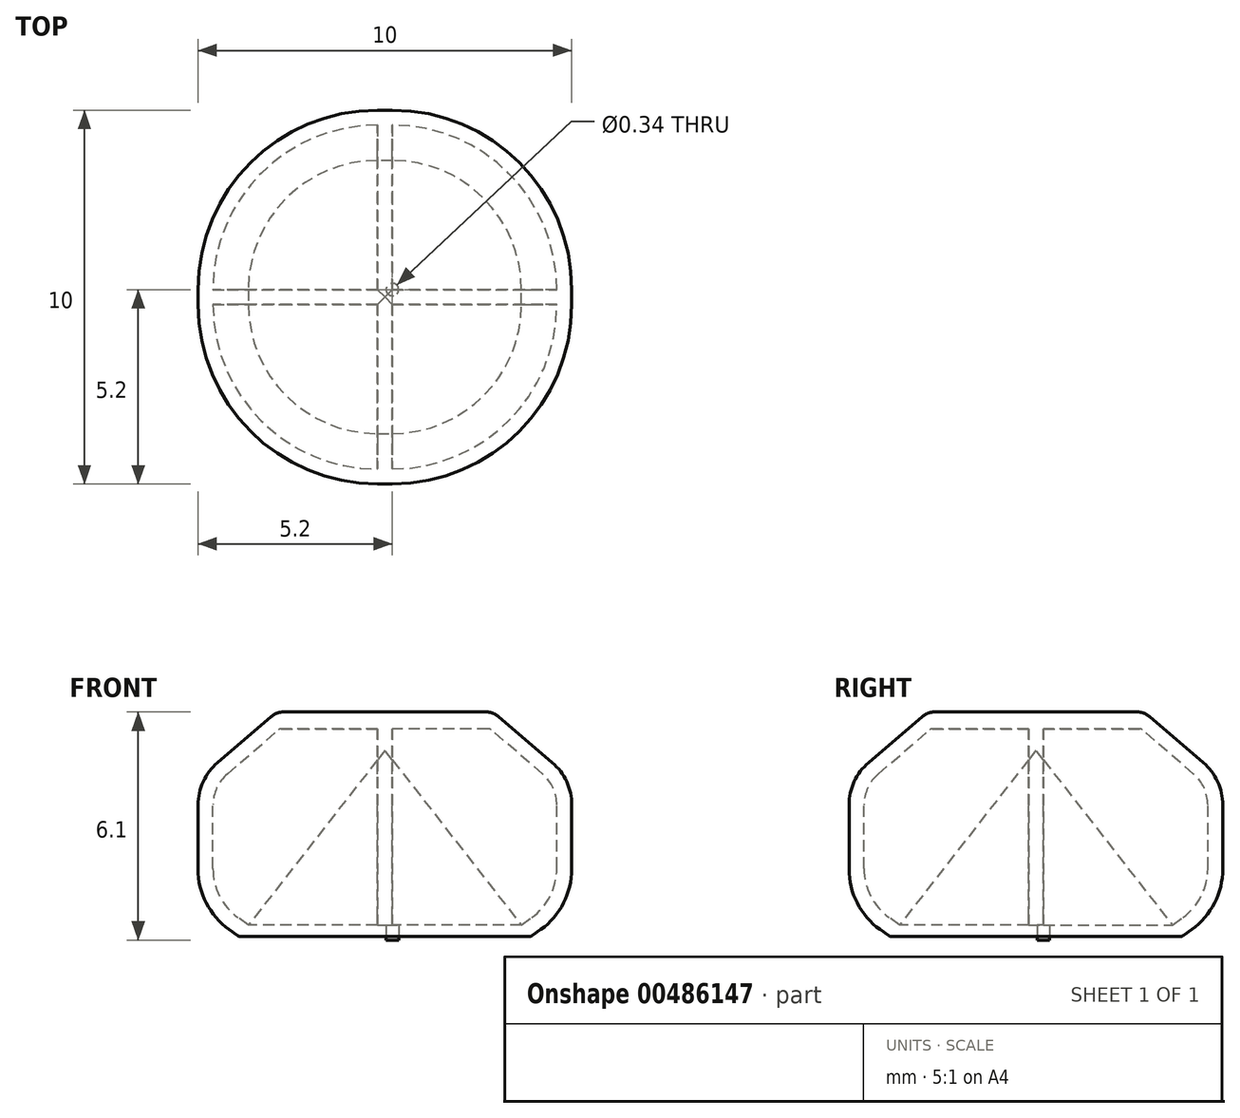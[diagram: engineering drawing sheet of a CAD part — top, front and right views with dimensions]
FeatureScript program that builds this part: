
annotation { "Feature Type Name" : "Feature", "Feature Type Description" : "" }
export const myFeature = defineFeature(function(context is Context, id is Id, definition is map)
    precondition{}
    {
        {
            assignVariable(context, id + "F0", {"name" : "l2", "anyValue" : 0.4});
        }
        {
            assignVariable(context, id + "F1", {"name" : "Scaf", "anyValue" : 0.65});
        }
        {
            var Q0;
            Q0=qCreatedBy(makeId("Front.planeOp"),FACE);
            var sketch = newSketch(context, id + "F2", { "sketchPlane" : qUnion([Q0])});
            skLineSegment(sketch, "E0", {"start": v(0, 0) * mm, "end": v(3.69, 0) * mm});
            skLineSegment(sketch, "E1", {"start": v(4.8, 1.8) * mm, "end": v(4.8, 3.51) * mm});
            skLineSegment(sketch, "E2", {"start": v(2.52, 6) * mm, "end": v(0, 6) * mm});
            skLineSegment(sketch, "E3", {"start": v(3.75, 0.02) * mm, "end": v(3.97, 0.18) * mm});
            skLineSegment(sketch, "E4", {"start": v(4.28, 4.65) * mm, "end": v(2.84, 5.88) * mm});
            skLineSegment(sketch, "E5", {"start": v(0, 0) * mm, "end": v(0, 0.3) * mm});
            skLineSegment(sketch, "E6", {"start": v(0, 0.3) * mm, "end": v(3.45, 0.3) * mm});
            skLineSegment(sketch, "E7", {"start": v(4.4, 1.81) * mm, "end": v(4.4, 3.51) * mm});
            skLineSegment(sketch, "E8", {"start": v(4.02, 4.35) * mm, "end": v(2.64, 5.53) * mm});
            skLineSegment(sketch, "E9", {"start": v(2.57, 5.55) * mm, "end": v(0, 5.55) * mm});
            skLineSegment(sketch, "E10", {"start": v(0, 5.55) * mm, "end": v(0, 6) * mm});
            skLineSegment(sketch, "E11", {"start": v(3.45, 0.3) * mm, "end": v(3.73, 0.5) * mm});
            skPoint(sketch, "E12.visualSharp", {"position": v(4.8, 0.78) * mm});
            skArc(sketch, "E12.filletArc", {"start": v(3.97, 0.18) * mm, "mid": v(4.58, 0.9) * mm, "end": v(4.8, 1.8) * mm});
            skPoint(sketch, "E13.visualSharp", {"position": v(4.8, 4.2) * mm});
            skArc(sketch, "E13.filletArc", {"start": v(4.8, 3.51) * mm, "mid": v(4.66, 4.14) * mm, "end": v(4.28, 4.65) * mm});
            skPoint(sketch, "E14.visualSharp", {"position": v(2.7, 6) * mm});
            skArc(sketch, "E14.filletArc", {"start": v(2.84, 5.88) * mm, "mid": v(2.69, 5.97) * mm, "end": v(2.52, 6) * mm});
            skPoint(sketch, "E15.visualSharp", {"position": v(2.61, 5.55) * mm});
            skArc(sketch, "E15.filletArc", {"start": v(2.64, 5.53) * mm, "mid": v(2.6, 5.54) * mm, "end": v(2.57, 5.55) * mm});
            skPoint(sketch, "E16.visualSharp", {"position": v(4.4, 4.02) * mm});
            skArc(sketch, "E16.filletArc", {"start": v(4.4, 3.51) * mm, "mid": v(4.3, 3.97) * mm, "end": v(4.02, 4.35) * mm});
            skPoint(sketch, "E17.visualSharp", {"position": v(4.4, 0.98) * mm});
            skArc(sketch, "E17.filletArc", {"start": v(3.73, 0.5) * mm, "mid": v(4.22, 1.08) * mm, "end": v(4.4, 1.81) * mm});
            skPoint(sketch, "E18.visualSharp", {"position": v(3.72, 0) * mm});
            skArc(sketch, "E18.filletArc", {"start": v(3.69, 0) * mm, "mid": v(3.72, 0) * mm, "end": v(3.75, 0.02) * mm});
            skSolve(sketch);
        }
        {
            var Q0;
            Q0=makeQuery(id+"F2.imprint","IMPRINT",FACE,{"disambiguationData":[TD([[makeQuery(id+"F2.imprint","IMPRINT",EDGE,{"derivedFrom":sQuery(id+"F2.wireOp",EDGE,"E0")}),1.0]])]});
            extrude(context, id + "F3", {"entities" : qUnion([Q0]), "depth" : (getVariable(context, 'l2')) * mm, "offsetDistance" : 25 * mm});
        }
        {
            var Q0;
            Q0=makeQuery(id+"F3.opExtrude","SWEPT_FACE",FACE,{"disambiguationData":[OSD([sQuery(id+"F2.wireOp",EDGE,"E10")])]});
            var Q1;
            Q1=sQuery(id+"F10.wireOp",EDGE,"E19");
            extrude(context, id + "F4", {"entities" : qUnion([Q0]), "operationType" : NewBodyOperationType.ADD, "surfaceEntities" : qUnion([Q1]), "depth" : (getVariable(context, 'Scaf')) * mm, "offsetDistance" : 25 * mm});
        }
        {
            var Q1;
            Q1=makeQuery(id+"F3.opExtrude","SWEPT_FACE",FACE,{"disambiguationData":[OSD([sQuery(id+"F2.wireOp",EDGE,"E9")])]});
            var Q2;
            Q2=makeQuery(id+"F3.opExtrude","SWEPT_FACE",FACE,{"disambiguationData":[OSD([sQuery(id+"F2.wireOp",EDGE,"E11")])]});
            loft(context, id + "F5", {"operationType" : NewBodyOperationType.ADD, "sheetProfilesArray" : [{ "sheetProfileEntities" : qUnion([Q1]) }, { "sheetProfileEntities" : qUnion([Q2]) }]});
        }
        {
            var Q1;
            Q1=makeQuery(id+"F3.opExtrude","SWEPT_FACE",FACE,{"disambiguationData":[OSD([sQuery(id+"F2.wireOp",EDGE,"E17.filletArc")])]});
            var Q2;
            Q2=makeQuery(id+"F3.opExtrude","SWEPT_FACE",FACE,{"disambiguationData":[OSD([sQuery(id+"F2.wireOp",EDGE,"E15.filletArc")])]});
            loft(context, id + "F6", {"operationType" : NewBodyOperationType.ADD, "sheetProfilesArray" : [{ "sheetProfileEntities" : qUnion([Q1]) }, { "sheetProfileEntities" : qUnion([Q2]) }]});
        }
        {
            var Q1;
            Q1=makeQuery(id+"F3.opExtrude","SWEPT_FACE",FACE,{"disambiguationData":[OSD([sQuery(id+"F2.wireOp",EDGE,"E8")])]});
            var Q2;
            Q2=makeQuery(id+"F3.opExtrude","SWEPT_FACE",FACE,{"disambiguationData":[OSD([sQuery(id+"F2.wireOp",EDGE,"E7")])]});
            loft(context, id + "F7", {"operationType" : NewBodyOperationType.ADD, "sheetProfilesArray" : [{ "sheetProfileEntities" : qUnion([Q1]) }, { "sheetProfileEntities" : qUnion([Q2]) }]});
        }
        {
            var Q0;
            Q0=makeQuery(id+"F7.opLoft","SWEPT_FACE",FACE,{"disambiguationData":[OSD([sQuery(id+"F2.wireOp",EDGE,"E7"),sQuery(id+"F2.wireOp",EDGE,"E8"),sQuery(id+"F2.wireOp",EDGE,"E16.filletArc")])]});
            extrude(context, id + "F8", {"entities" : qUnion([Q0]), "operationType" : NewBodyOperationType.ADD, "depth" : .2 * mm, "offsetDistance" : 25 * mm});
        }
        {
            var Q0;
            Q0=makeQuery(id+"F2.imprint","IMPRINT",FACE,{"disambiguationData":[TD([[makeQuery(id+"F2.imprint","IMPRINT",EDGE,{"derivedFrom":sQuery(id+"F2.wireOp",EDGE,"E0")}),1.0]])]});
            var Q1;
            Q1=sQuery(id+"F2.wireOp",EDGE,"E10");
            revolve(context, id + "F9", {"operationType" : NewBodyOperationType.ADD, "entities" : qUnion([Q0]), "axis" : qUnion([Q1]), "revolveType" : RevolveType.ONE_DIRECTION, "angle" : 90 * degree});
        }
        {
            var Q0;
            Q0=qCreatedBy(makeId("Front.planeOp"),FACE);
            var sketch = newSketch(context, id + "F10", { "sketchPlane" : qUnion([Q0])});
            skLineSegment(sketch, "E19", {"start": v(0, 0) * mm, "end": v(-0.4, 0) * mm});
            skLineSegment(sketch, "E20", {"start": v(-0.4, 0) * mm, "end": v(-0.4, 0.13) * mm});
            skSolve(sketch);
        }
        {
            var Q0;
            Q0=qCreatedBy(makeId("Front.planeOp"),FACE);
            cPlane(context, id + "F11", {"entities" : qUnion([Q0]), "cplaneType" : CPlaneType.OFFSET, "offset" : (getVariable(context, 'l2') / 2) * mm, "width" : 150 * mm, "height" : 150 * mm});
        }
        {
            var Q0;
            Q0=qCreatedBy(id+"F11.planeOp",FACE);
            var sketch = newSketch(context, id + "F12", { "sketchPlane" : qUnion([Q0])});
            skLineSegment(sketch, "E21", {"start": v(0, 0.03) * mm, "end": v(-0.2, 0.03) * mm});
            skLineSegment(sketch, "E22", {"start": v(-0.2, 0.03) * mm, "end": v(-0.2, 0.22) * mm});
            skLineSegment(sketch, "E23", {"start": v(0, 0.03) * mm, "end": v(0, 0.08) * mm});
            skLineSegment(sketch, "E24", {"start": v(0, 0.03) * mm, "end": v(0, 0.14) * mm});
            skPoint(sketch, "E24.endSnap0", {"position": v(0, 0.05) * mm});
            skSolve(sketch);
        }
        {
            var Q0;
            Q0=makeQuery(id+"F3.opExtrude","SWEPT_BODY",BODY,{"disambiguationData":[OSD([sQuery(id+"F2.wireOp",EDGE,"E0"),sQuery(id+"F2.wireOp",EDGE,"E1"),sQuery(id+"F2.wireOp",EDGE,"E2"),sQuery(id+"F2.wireOp",EDGE,"E3"),sQuery(id+"F2.wireOp",EDGE,"E4"),sQuery(id+"F2.wireOp",EDGE,"E5"),sQuery(id+"F2.wireOp",EDGE,"E6"),sQuery(id+"F2.wireOp",EDGE,"E7"),sQuery(id+"F2.wireOp",EDGE,"E8"),sQuery(id+"F2.wireOp",EDGE,"E9"),sQuery(id+"F2.wireOp",EDGE,"E10"),sQuery(id+"F2.wireOp",EDGE,"E11"),sQuery(id+"F2.wireOp",EDGE,"E12.filletArc"),sQuery(id+"F2.wireOp",EDGE,"E13.filletArc"),sQuery(id+"F2.wireOp",EDGE,"E14.filletArc"),sQuery(id+"F2.wireOp",EDGE,"E15.filletArc"),sQuery(id+"F2.wireOp",EDGE,"E16.filletArc"),sQuery(id+"F2.wireOp",EDGE,"E17.filletArc"),sQuery(id+"F2.wireOp",EDGE,"E18.filletArc")])]});
            var Q1;
            Q1=sQuery(id+"F12.wireOp",EDGE,"E22");
            transform(context, id + "F13", {"entities" : qUnion([Q0]), "transformType" : TransformType.ROTATION, "transformAxis" : qUnion([Q1]), "angle" : 90 * degree, "oppositeDirection" : true, "makeCopy" : true});
        }
        {
            var Q0;
            Q0=makeQuery(id+"F3.opExtrude","SWEPT_BODY",BODY,{"disambiguationData":[OSD([sQuery(id+"F2.wireOp",EDGE,"E0"),sQuery(id+"F2.wireOp",EDGE,"E1"),sQuery(id+"F2.wireOp",EDGE,"E2"),sQuery(id+"F2.wireOp",EDGE,"E3"),sQuery(id+"F2.wireOp",EDGE,"E4"),sQuery(id+"F2.wireOp",EDGE,"E5"),sQuery(id+"F2.wireOp",EDGE,"E6"),sQuery(id+"F2.wireOp",EDGE,"E7"),sQuery(id+"F2.wireOp",EDGE,"E8"),sQuery(id+"F2.wireOp",EDGE,"E9"),sQuery(id+"F2.wireOp",EDGE,"E10"),sQuery(id+"F2.wireOp",EDGE,"E11"),sQuery(id+"F2.wireOp",EDGE,"E12.filletArc"),sQuery(id+"F2.wireOp",EDGE,"E13.filletArc"),sQuery(id+"F2.wireOp",EDGE,"E14.filletArc"),sQuery(id+"F2.wireOp",EDGE,"E15.filletArc"),sQuery(id+"F2.wireOp",EDGE,"E16.filletArc"),sQuery(id+"F2.wireOp",EDGE,"E17.filletArc"),sQuery(id+"F2.wireOp",EDGE,"E18.filletArc")])]});
            var Q1;
            Q1=makeQuery(id+"F13.opPattern","COPY",BODY,{"derivedFrom":makeQuery(id+"F3.opExtrude","SWEPT_BODY",BODY,{"disambiguationData":[OSD([sQuery(id+"F2.wireOp",EDGE,"E0"),sQuery(id+"F2.wireOp",EDGE,"E1"),sQuery(id+"F2.wireOp",EDGE,"E2"),sQuery(id+"F2.wireOp",EDGE,"E3"),sQuery(id+"F2.wireOp",EDGE,"E4"),sQuery(id+"F2.wireOp",EDGE,"E5"),sQuery(id+"F2.wireOp",EDGE,"E6"),sQuery(id+"F2.wireOp",EDGE,"E7"),sQuery(id+"F2.wireOp",EDGE,"E8"),sQuery(id+"F2.wireOp",EDGE,"E9"),sQuery(id+"F2.wireOp",EDGE,"E10"),sQuery(id+"F2.wireOp",EDGE,"E11"),sQuery(id+"F2.wireOp",EDGE,"E12.filletArc"),sQuery(id+"F2.wireOp",EDGE,"E13.filletArc"),sQuery(id+"F2.wireOp",EDGE,"E14.filletArc"),sQuery(id+"F2.wireOp",EDGE,"E15.filletArc"),sQuery(id+"F2.wireOp",EDGE,"E16.filletArc"),sQuery(id+"F2.wireOp",EDGE,"E17.filletArc"),sQuery(id+"F2.wireOp",EDGE,"E18.filletArc")])]}),"instanceName":"1"});
            booleanBodies(context, id + "F14", {"operationType" : BooleanOperationType.UNION, "tools" : qUnion([Q0, Q1])});
        }
        {
            var Q0;
            Q0=makeQuery(id+"F3.opExtrude","SWEPT_BODY",BODY,{"disambiguationData":[OSD([sQuery(id+"F2.wireOp",EDGE,"E0"),sQuery(id+"F2.wireOp",EDGE,"E1"),sQuery(id+"F2.wireOp",EDGE,"E2"),sQuery(id+"F2.wireOp",EDGE,"E3"),sQuery(id+"F2.wireOp",EDGE,"E4"),sQuery(id+"F2.wireOp",EDGE,"E5"),sQuery(id+"F2.wireOp",EDGE,"E6"),sQuery(id+"F2.wireOp",EDGE,"E7"),sQuery(id+"F2.wireOp",EDGE,"E8"),sQuery(id+"F2.wireOp",EDGE,"E9"),sQuery(id+"F2.wireOp",EDGE,"E10"),sQuery(id+"F2.wireOp",EDGE,"E11"),sQuery(id+"F2.wireOp",EDGE,"E12.filletArc"),sQuery(id+"F2.wireOp",EDGE,"E13.filletArc"),sQuery(id+"F2.wireOp",EDGE,"E14.filletArc"),sQuery(id+"F2.wireOp",EDGE,"E15.filletArc"),sQuery(id+"F2.wireOp",EDGE,"E16.filletArc"),sQuery(id+"F2.wireOp",EDGE,"E17.filletArc"),sQuery(id+"F2.wireOp",EDGE,"E18.filletArc")])]});
            var Q1;
            Q1=sQuery(id+"F12.wireOp",EDGE,"E22");
            transform(context, id + "F15", {"entities" : qUnion([Q0]), "transformType" : TransformType.ROTATION, "transformAxis" : qUnion([Q1]), "angle" : 180 * degree, "makeCopy" : true});
        }
        {
            var Q0;
            Q0=makeQuery(id+"F3.opExtrude","SWEPT_BODY",BODY,{"disambiguationData":[OSD([sQuery(id+"F2.wireOp",EDGE,"E0"),sQuery(id+"F2.wireOp",EDGE,"E1"),sQuery(id+"F2.wireOp",EDGE,"E2"),sQuery(id+"F2.wireOp",EDGE,"E3"),sQuery(id+"F2.wireOp",EDGE,"E4"),sQuery(id+"F2.wireOp",EDGE,"E5"),sQuery(id+"F2.wireOp",EDGE,"E6"),sQuery(id+"F2.wireOp",EDGE,"E7"),sQuery(id+"F2.wireOp",EDGE,"E8"),sQuery(id+"F2.wireOp",EDGE,"E9"),sQuery(id+"F2.wireOp",EDGE,"E10"),sQuery(id+"F2.wireOp",EDGE,"E11"),sQuery(id+"F2.wireOp",EDGE,"E12.filletArc"),sQuery(id+"F2.wireOp",EDGE,"E13.filletArc"),sQuery(id+"F2.wireOp",EDGE,"E14.filletArc"),sQuery(id+"F2.wireOp",EDGE,"E15.filletArc"),sQuery(id+"F2.wireOp",EDGE,"E16.filletArc"),sQuery(id+"F2.wireOp",EDGE,"E17.filletArc"),sQuery(id+"F2.wireOp",EDGE,"E18.filletArc")])]});
            var Q1;
            Q1=makeQuery(id+"F15.opPattern","COPY",BODY,{"derivedFrom":makeQuery(id+"F3.opExtrude","SWEPT_BODY",BODY,{"disambiguationData":[OSD([sQuery(id+"F2.wireOp",EDGE,"E0"),sQuery(id+"F2.wireOp",EDGE,"E1"),sQuery(id+"F2.wireOp",EDGE,"E2"),sQuery(id+"F2.wireOp",EDGE,"E3"),sQuery(id+"F2.wireOp",EDGE,"E4"),sQuery(id+"F2.wireOp",EDGE,"E5"),sQuery(id+"F2.wireOp",EDGE,"E6"),sQuery(id+"F2.wireOp",EDGE,"E7"),sQuery(id+"F2.wireOp",EDGE,"E8"),sQuery(id+"F2.wireOp",EDGE,"E9"),sQuery(id+"F2.wireOp",EDGE,"E10"),sQuery(id+"F2.wireOp",EDGE,"E11"),sQuery(id+"F2.wireOp",EDGE,"E12.filletArc"),sQuery(id+"F2.wireOp",EDGE,"E13.filletArc"),sQuery(id+"F2.wireOp",EDGE,"E14.filletArc"),sQuery(id+"F2.wireOp",EDGE,"E15.filletArc"),sQuery(id+"F2.wireOp",EDGE,"E16.filletArc"),sQuery(id+"F2.wireOp",EDGE,"E17.filletArc"),sQuery(id+"F2.wireOp",EDGE,"E18.filletArc")])]}),"instanceName":"1"});
            booleanBodies(context, id + "F16", {"operationType" : BooleanOperationType.UNION, "tools" : qUnion([Q0, Q1])});
        }
        {
            var Q0;
            {var subQ0=sQuery(id+"F2.wireOp",EDGE,"E18.filletArc");var subQ1=sQuery(id+"F2.wireOp",EDGE,"E17.filletArc");var subQ2=sQuery(id+"F2.wireOp",EDGE,"E16.filletArc");var subQ3=sQuery(id+"F2.wireOp",EDGE,"E15.filletArc");var subQ4=sQuery(id+"F2.wireOp",EDGE,"E14.filletArc");var subQ5=sQuery(id+"F2.wireOp",EDGE,"E13.filletArc");var subQ6=sQuery(id+"F2.wireOp",EDGE,"E12.filletArc");var subQ7=sQuery(id+"F2.wireOp",EDGE,"E11");var subQ8=sQuery(id+"F2.wireOp",EDGE,"E10");var subQ9=sQuery(id+"F2.wireOp",EDGE,"E9");var subQ10=sQuery(id+"F2.wireOp",EDGE,"E8");var subQ11=sQuery(id+"F2.wireOp",EDGE,"E7");var subQ12=sQuery(id+"F2.wireOp",EDGE,"E6");var subQ13=sQuery(id+"F2.wireOp",EDGE,"E5");var subQ14=sQuery(id+"F2.wireOp",EDGE,"E4");var subQ15=sQuery(id+"F2.wireOp",EDGE,"E3");var subQ16=sQuery(id+"F2.wireOp",EDGE,"E2");var subQ17=sQuery(id+"F2.wireOp",EDGE,"E1");var subQ18=sQuery(id+"F2.wireOp",EDGE,"E0");var subQ19=makeQuery(id+"F9.opRevolve","CAP_FACE",FACE,{"disambiguationData":[OSD([subQ18,subQ17,subQ16,subQ15,subQ14,subQ13,subQ12,subQ11,subQ10,subQ9,subQ8,subQ7,subQ6,subQ5,subQ4,subQ3,subQ2,subQ1,subQ0])],"isStart":false});var subQ32=makeQuery(id+"F3.opExtrude","SWEPT_FACE",FACE,{"disambiguationData":[OSD([subQ13])]});var subQ33=makeQuery(id+"F3.opExtrude","SWEPT_FACE",FACE,{"disambiguationData":[OSD([subQ8])]});var subQ35=makeQuery(id+"F3.opExtrude","SWEPT_FACE",FACE,{"disambiguationData":[OSD([subQ16])]});Q0=makeQuery(id+"F15.opPattern","COPY",FACE,{"derivedFrom":makeQuery(id+"F14.opBoolean","SPLIT",FACE,{"disambiguationData":[TD([subQ35])],"derivedFrom":makeQuery(id+"F13.opPattern","COPY",FACE,{"derivedFrom":makeQuery(id+"F9.boolean.opBoolean","MERGE",FACE,{"derivedFrom":[subQ32,subQ33,subQ19]}),"instanceName":"1"})}),"instanceName":"1"});}
            extrude(context, id + "F17", {"entities" : qUnion([Q0]), "operationType" : NewBodyOperationType.ADD, "depth" : (getVariable(context, 'l2') * 1.5) * mm, "offsetDistance" : 25 * mm});
        }
        {
            var Q0;
            {var subQ0=sQuery(id+"F2.wireOp",EDGE,"E0");var subQ1=makeQuery(id+"F9.boolean.opBoolean","MERGE",FACE,{"derivedFrom":[makeQuery(id+"F3.opExtrude","SWEPT_FACE",FACE,{"disambiguationData":[OSD([subQ0])]}),makeQuery(id+"F9.opRevolve","SWEPT_FACE",FACE,{"disambiguationData":[OSD([subQ0])]})]});var subQ2=makeQuery(id+"F14.opBoolean","MERGE",FACE,{"derivedFrom":[subQ1,makeQuery(id+"F13.opPattern","COPY",FACE,{"derivedFrom":subQ1,"instanceName":"1"})]});Q0=makeQuery(id+"F17.boolean.opBoolean","MERGE",FACE,{"derivedFrom":[makeQuery(id+"F16.opBoolean","MERGE",FACE,{"derivedFrom":[subQ2,makeQuery(id+"F15.opPattern","COPY",FACE,{"derivedFrom":subQ2,"instanceName":"1"})]}),makeQuery(id+"F17.opExtrude","SWEPT_FACE",FACE,{"disambiguationData":[OSD([subQ0,sQuery(id+"F2.wireOp",EDGE,"E5")])]})]});}
            var sketch = newSketch(context, id + "F18", { "sketchPlane" : qUnion([Q0])});
            skCircle(sketch, "E25", {"center": v(0, 0) * mm, "radius": 0.17 * mm});
            skSolve(sketch);
        }
        {
            var Q0;
            Q0=makeQuery(id+"F18.imprint","IMPRINT",FACE,{"disambiguationData":[TD([[makeQuery(id+"F18.imprint","IMPRINT",EDGE,{"derivedFrom":sQuery(id+"F18.wireOp",EDGE,"E25")}),-1.0]])]});
            cPlane(context, id + "F19", {"entities" : qUnion([Q0]), "cplaneType" : CPlaneType.OFFSET, "offset" : .1 * mm, "width" : 150 * mm, "height" : 150 * mm});
        }
        {
            var Q0;
            Q0=qCreatedBy(id+"F19.planeOp",FACE);
            var sketch = newSketch(context, id + "F20", { "sketchPlane" : qUnion([Q0])});
            skLineSegment(sketch, "E26", {"start": v(0, 0) * mm, "end": v(-0.33, -0.11) * mm});
            skSolve(sketch);
        }
        {
            var Q1;
            Q1=makeQuery(id+"F18.imprint","IMPRINT",FACE,{"disambiguationData":[TD([[makeQuery(id+"F18.imprint","IMPRINT",EDGE,{"derivedFrom":sQuery(id+"F18.wireOp",EDGE,"E25")}),1.0]])]});
            var Q2;
            Q2=sQuery(id+"F20.wireOp",VERTEX,"E26.start");
            loft(context, id + "F21", {"operationType" : NewBodyOperationType.ADD, "sheetProfilesArray" : [{ "sheetProfileEntities" : qUnion([Q1]) }, { "sheetProfileEntities" : qUnion([Q2]) }]});
        }
        {
            var Q0;
            Q0=makeQuery(id+"F18.imprint","IMPRINT",FACE,{"disambiguationData":[TD([[makeQuery(id+"F18.imprint","IMPRINT",EDGE,{"derivedFrom":sQuery(id+"F18.wireOp",EDGE,"E25")}),1.0]])]});
            extrude(context, id + "F22", {"entities" : qUnion([Q0]), "operationType" : NewBodyOperationType.ADD, "depth" : .1 * mm, "offsetDistance" : 25 * mm});
        }
        {
            var Q0;
            Q0=makeQuery(id+"F18.imprint","IMPRINT",FACE,{"disambiguationData":[TD([[makeQuery(id+"F18.imprint","IMPRINT",EDGE,{"derivedFrom":sQuery(id+"F18.wireOp",EDGE,"E25")}),1.0]])]});
            extrude(context, id + "F23", {"entities" : qUnion([Q0]), "operationType" : NewBodyOperationType.REMOVE, "oppositeDirection" : true, "depth" : 1 * mm, "offsetDistance" : 25 * mm});
        }
    });
